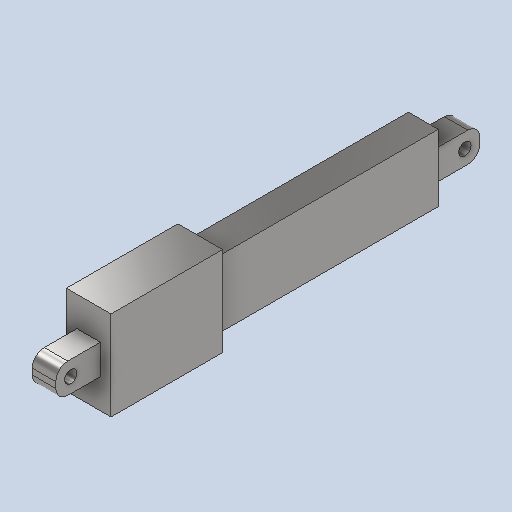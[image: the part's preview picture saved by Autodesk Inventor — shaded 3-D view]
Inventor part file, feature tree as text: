
AUTODESK INVENTOR PART (.ipt)
format: ipt  version: 2024 (Build 280153000, 153)  size: 291,328 bytes
history: native  units: mm
features: extrude x5, sketch x5, other x2, mirror x2, fillet x1
ambient origin geometry x8: Origin, YZ Plane, XZ Plane, XY Plane, X Axis, Y Axis, Z Axis, Center Point
bodies: Body1 (feature_tree)
feature tree (15):
  other  "솔리드1"
  extrude  "돌출1"  Depth=15.0mm
  extrude  "돌출2"  Depth=30.0mm
  extrude  "돌출3"  Depth=15.0mm
  extrude  "돌출4"  Depth=7.5mm
  extrude  "돌출5"  Depth=37.5mm TaperAngle=0.0deg
  other  "작업 평면1"
  mirror  "미러1"
  mirror  "미러2"
  fillet  "모깎기1"  Radius=10.0mm
  sketch  "스케치1"
  sketch  "스케치2"
  sketch  "스케치3"
  sketch  "스케치4"
  sketch  "스케치5"
